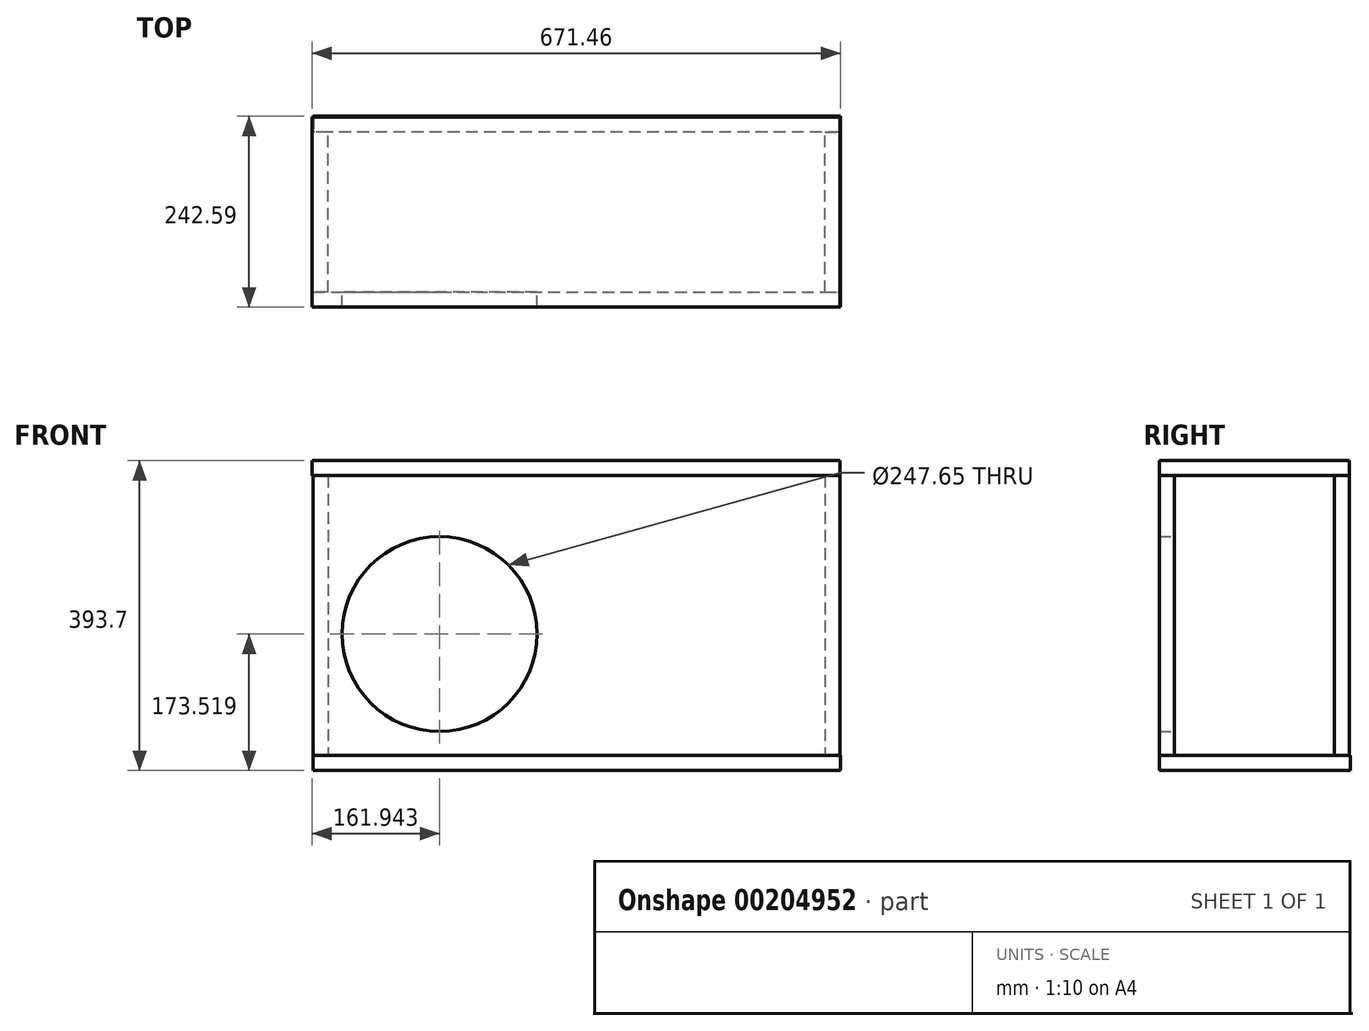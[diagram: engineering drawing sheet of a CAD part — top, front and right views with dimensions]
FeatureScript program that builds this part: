
annotation { "Feature Type Name" : "Feature", "Feature Type Description" : "" }
export const myFeature = defineFeature(function(context is Context, id is Id, definition is map)
    precondition{}
    {
        {
            var Q0;
            Q0=qCreatedBy(makeId("Front.planeOp"),FACE);
            var sketch = newSketch(context, id + "F0", { "sketchPlane" : qUnion([Q0])});
            skLineSegment(sketch, "E0.bottom", {"start": v(-334.68, 177.8) * mm, "end": v(334.68, 177.8) * mm});
            skLineSegment(sketch, "E0.top", {"start": v(-334.68, -177.8) * mm, "end": v(334.68, -177.8) * mm});
            skLineSegment(sketch, "E0.left", {"start": v(-334.68, 177.8) * mm, "end": v(-334.68, -177.8) * mm});
            skLineSegment(sketch, "E0.right", {"start": v(334.68, 177.8) * mm, "end": v(334.68, -177.8) * mm});
            skPoint(sketch, "E0.middle", {"position": v(0, 0) * mm});
            skCircle(sketch, "E1", {"center": v(-173.78, -23.33) * mm, "radius": 123.83 * mm});
            skSolve(sketch);
        }
        {
            var Q0;
            Q0=makeQuery(id+"F0.imprint","IMPRINT",FACE,{"disambiguationData":[TD([[makeQuery(id+"F0.imprint","IMPRINT",EDGE,{"derivedFrom":sQuery(id+"F0.wireOp",EDGE,"E0.bottom")}),-1.0]])]});
            extrude(context, id + "F1", {"entities" : qUnion([Q0]), "depth" : 19.05 * mm});
        }
        {
            var Q0;
            Q0=makeQuery(id+"F1.opExtrude","SWEPT_FACE",FACE,{"disambiguationData":[OSD([sQuery(id+"F0.wireOp",EDGE,"E0.right")])]});
            var sketch = newSketch(context, id + "F2", { "sketchPlane" : qUnion([Q0])});
            skLineSegment(sketch, "E2.bottom", {"start": v(0, 177.8) * mm, "end": v(203.2, 177.8) * mm});
            skLineSegment(sketch, "E2.top", {"start": v(0, -177.8) * mm, "end": v(203.2, -177.8) * mm});
            skLineSegment(sketch, "E2.left", {"start": v(0, 177.8) * mm, "end": v(0, -177.8) * mm});
            skLineSegment(sketch, "E2.right", {"start": v(203.2, 177.8) * mm, "end": v(203.2, -177.8) * mm});
            skSolve(sketch);
        }
        {
            var Q0;
            Q0 = qSketchRegion(id + "F2", true);
            extrude(context, id + "F3", {"entities" : qUnion([Q0]), "oppositeDirection" : true, "depth" : 19.05 * mm});
        }
        {
            var Q0;
            Q0=makeQuery(id+"F1.opExtrude","SWEPT_FACE",FACE,{"disambiguationData":[OSD([sQuery(id+"F0.wireOp",EDGE,"E0.left")])]});
            var sketch = newSketch(context, id + "F4", { "sketchPlane" : qUnion([Q0])});
            skLineSegment(sketch, "E3.bottom", {"start": v(0, 177.8) * mm, "end": v(-203.2, 177.8) * mm});
            skLineSegment(sketch, "E3.top", {"start": v(0, -177.8) * mm, "end": v(-203.2, -177.8) * mm});
            skLineSegment(sketch, "E3.left", {"start": v(0, 177.8) * mm, "end": v(0, -177.8) * mm});
            skLineSegment(sketch, "E3.right", {"start": v(-203.2, 177.8) * mm, "end": v(-203.2, -177.8) * mm});
            skSolve(sketch);
        }
        {
            var Q0;
            Q0 = qSketchRegion(id + "F4", true);
            extrude(context, id + "F5", {"entities" : qUnion([Q0]), "oppositeDirection" : true, "depth" : 19.05 * mm});
        }
        {
            var Q0;
            Q0=makeQuery(id+"F3.opExtrude","SWEPT_FACE",FACE,{"disambiguationData":[OSD([sQuery(id+"F2.wireOp",EDGE,"E2.right")])]});
            var sketch = newSketch(context, id + "F6", { "sketchPlane" : qUnion([Q0])});
            skLineSegment(sketch, "E4.bottom", {"start": v(-334.68, 177.8) * mm, "end": v(334, 177.8) * mm});
            skLineSegment(sketch, "E4.top", {"start": v(-334.68, -177.8) * mm, "end": v(334, -177.8) * mm});
            skLineSegment(sketch, "E4.left", {"start": v(-334.68, 177.8) * mm, "end": v(-334.68, -177.8) * mm});
            skLineSegment(sketch, "E4.right", {"start": v(334, 177.8) * mm, "end": v(334, -177.8) * mm});
            skSolve(sketch);
        }
        {
            var Q0;
            Q0 = qSketchRegion(id + "F6", true);
            extrude(context, id + "F7", {"entities" : qUnion([Q0]), "depth" : 19.05 * mm});
        }
        {
            var Q0;
            Q0=makeQuery(id+"F1.opExtrude","SWEPT_FACE",FACE,{"disambiguationData":[OSD([sQuery(id+"F0.wireOp",EDGE,"E0.top")])]});
            var sketch = newSketch(context, id + "F8", { "sketchPlane" : qUnion([Q0])});
            skLineSegment(sketch, "E5.bottom", {"start": v(-334.68, 19.05) * mm, "end": v(335.74, 19.05) * mm});
            skLineSegment(sketch, "E5.top", {"start": v(-334.68, -223.43) * mm, "end": v(335.74, -223.43) * mm});
            skLineSegment(sketch, "E5.left", {"start": v(-334.68, 19.05) * mm, "end": v(-334.68, -223.43) * mm});
            skLineSegment(sketch, "E5.right", {"start": v(335.74, 19.05) * mm, "end": v(335.74, -223.43) * mm});
            skSolve(sketch);
        }
        {
            var Q0;
            Q0 = qSketchRegion(id + "F8", true);
            extrude(context, id + "F9", {"entities" : qUnion([Q0]), "depth" : 19.05 * mm});
        }
        {
            var Q0;
            Q0=makeQuery(id+"F7.opExtrude","SWEPT_FACE",FACE,{"disambiguationData":[OSD([sQuery(id+"F6.wireOp",EDGE,"E4.bottom")])]});
            var sketch = newSketch(context, id + "F10", { "sketchPlane" : qUnion([Q0])});
            skLineSegment(sketch, "E6.bottom", {"start": v(334.68, 222.25) * mm, "end": v(-335.72, 222.25) * mm});
            skLineSegment(sketch, "E6.top", {"start": v(334.68, -19.16) * mm, "end": v(-335.72, -19.16) * mm});
            skLineSegment(sketch, "E6.left", {"start": v(334.68, 222.25) * mm, "end": v(334.68, -19.16) * mm});
            skLineSegment(sketch, "E6.right", {"start": v(-335.72, 222.25) * mm, "end": v(-335.72, -19.16) * mm});
            skSolve(sketch);
        }
        {
            var Q0;
            Q0 = qSketchRegion(id + "F10", true);
            extrude(context, id + "F11", {"entities" : qUnion([Q0]), "depth" : 19.05 * mm});
        }
    });
